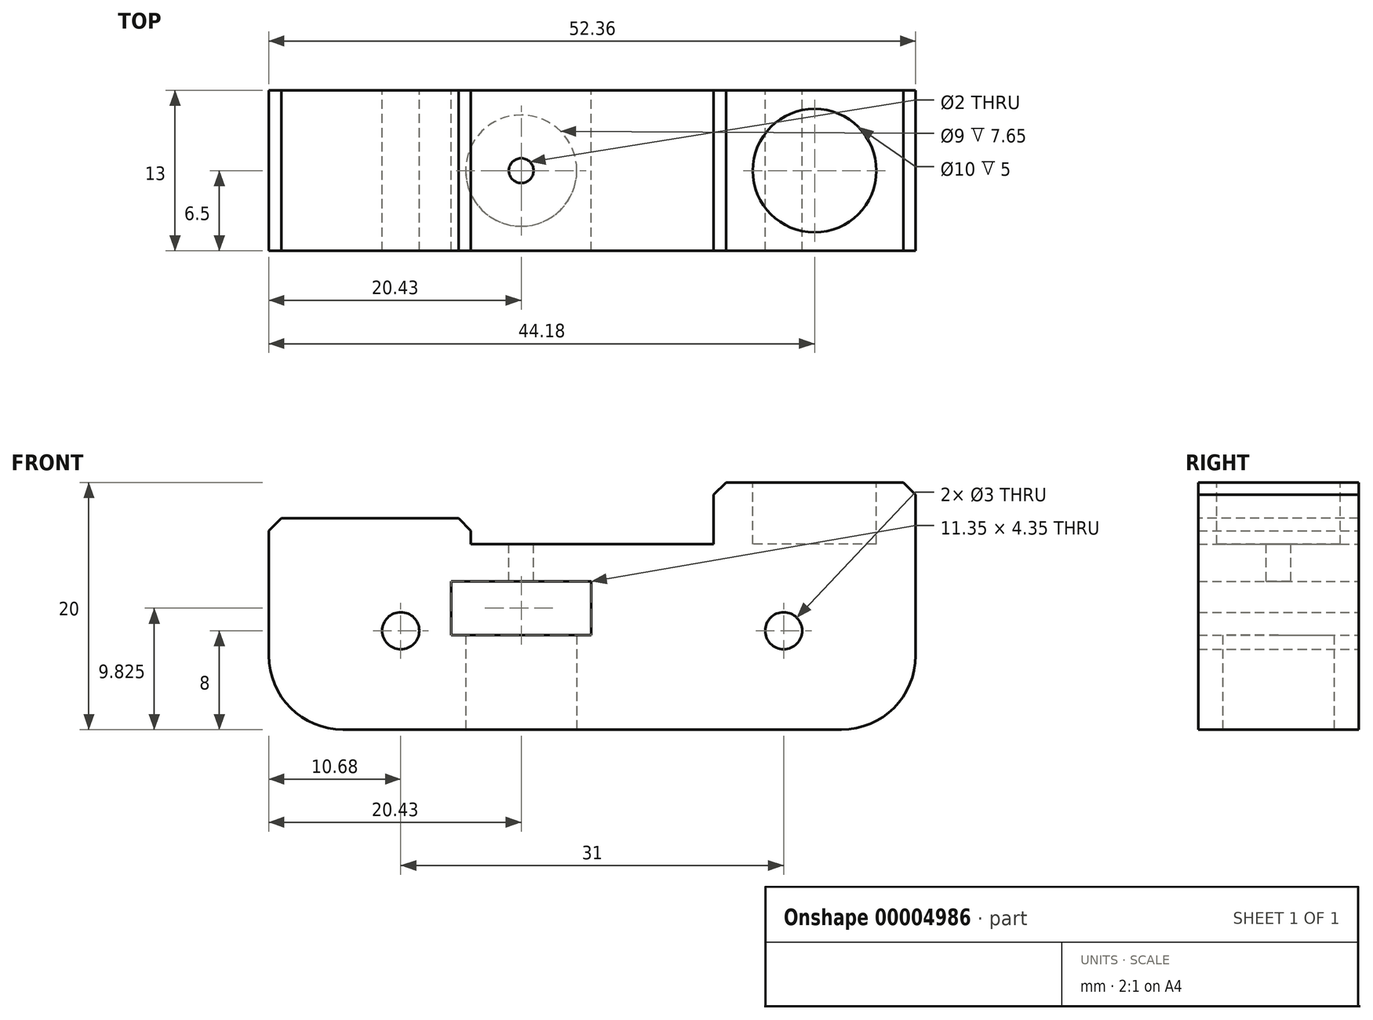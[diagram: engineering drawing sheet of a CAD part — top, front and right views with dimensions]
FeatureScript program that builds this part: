
annotation { "Feature Type Name" : "Feature", "Feature Type Description" : "" }
export const myFeature = defineFeature(function(context is Context, id is Id, definition is map)
    precondition{}
    {
        {
            var Q0;
            Q0=qCreatedBy(makeId("Front.planeOp"),FACE);
            var sketch = newSketch(context, id + "F0", { "sketchPlane" : qUnion([Q0])});
            skLineSegment(sketch, "E0", {"start": v(0, 0) * mm, "end": v(31, 0) * mm, "construction": true});
            skLineSegment(sketch, "E1", {"start": v(0, 0) * mm, "end": v(0, 31) * mm, "construction": true});
            skPoint(sketch, "E2", {"position": v(0, 10.1) * mm});
            skCircle(sketch, "E3", {"center": v(0, 0) * mm, "radius": 1.5 * mm});
            skCircle(sketch, "E4", {"center": v(31, 0) * mm, "radius": 1.5 * mm});
            skLineSegment(sketch, "E5", {"start": v(15.5, 0) * mm, "end": v(15.5, 31) * mm, "construction": true});
            skLineSegment(sketch, "E6", {"start": v(9.75, 0) * mm, "end": v(9.75, 33.75) * mm, "construction": true});
            skArc(sketch, "E7", {"start": v(0, 10.1) * mm, "mid": v(17.8, 20.04) * mm, "end": v(18.66, 40.41) * mm, "construction": true});
            skLineSegment(sketch, "E8", {"start": v(33.5, 41.53) * mm, "end": v(33.5, -19.25) * mm, "construction": true});
            skCircle(sketch, "E9", {"center": v(15.5, 15.5) * mm, "radius": 7.5 * mm, "construction": true});
            skLineSegment(sketch, "E10", {"start": v(-10.68, 9.1) * mm, "end": v(5.67, 9.1) * mm});
            skLineSegment(sketch, "E11", {"start": v(5.67, 9.1) * mm, "end": v(5.67, 7) * mm});
            skLineSegment(sketch, "E12", {"start": v(5.67, 7) * mm, "end": v(25.32, 7) * mm});
            skLineSegment(sketch, "E13", {"start": v(25.32, 7) * mm, "end": v(25.32, 12) * mm});
            skLineSegment(sketch, "E14", {"start": v(25.32, 12) * mm, "end": v(41.68, 12) * mm});
            skPoint(sketch, "E15", {"position": v(33.5, 12) * mm});
            skLineSegment(sketch, "E16", {"start": v(-10.68, 9.1) * mm, "end": v(-10.68, -8) * mm});
            skLineSegment(sketch, "E17", {"start": v(-10.68, -8) * mm, "end": v(41.68, -8) * mm});
            skLineSegment(sketch, "E18", {"start": v(41.68, -8) * mm, "end": v(41.68, 12) * mm});
            skPoint(sketch, "E19", {"position": v(15.5, 8) * mm});
            skLineSegment(sketch, "E20.bottom", {"start": v(4.08, 4) * mm, "end": v(15.42, 4) * mm});
            skLineSegment(sketch, "E20.top", {"start": v(4.08, -0.35) * mm, "end": v(15.42, -0.35) * mm});
            skLineSegment(sketch, "E20.left", {"start": v(4.08, 4) * mm, "end": v(4.08, -0.35) * mm});
            skLineSegment(sketch, "E20.right", {"start": v(15.43, 4) * mm, "end": v(15.43, -0.35) * mm});
            skSolve(sketch);
        }
        {
            var Q0;
            Q0 = qSketchRegion(id + "F0", true);
            extrude(context, id + "F1", {"entities" : qUnion([Q0]), "depth" : 13 * mm, "symmetric" : true});
        }
        {
            var Q0;
            Q0=makeQuery(id+"F1.opExtrude","SWEPT_FACE",FACE,{"disambiguationData":[OSD([sQuery(id+"F0.wireOp",EDGE,"E12")])]});
            var sketch = newSketch(context, id + "F2", { "sketchPlane" : qUnion([Q0])});
            skLineSegment(sketch, "E21.0", {"start": v(4.08, -6.5) * mm, "end": v(15.43, -6.5) * mm, "construction": true});
            skLineSegment(sketch, "E22", {"start": v(9.75, -6.5) * mm, "end": v(9.75, 6.5) * mm, "construction": true});
            skCircle(sketch, "E23", {"center": v(9.75, 0) * mm, "radius": 1 * mm});
            skSolve(sketch);
        }
        {
            var Q0;
            Q0 = qSketchRegion(id + "F2", true);
            extrude(context, id + "F3", {"entities" : qUnion([Q0]), "operationType" : NewBodyOperationType.REMOVE, "endBound" : BoundingType.THROUGH_ALL, "oppositeDirection" : true, "depth" : 25 * mm});
        }
        {
            var Q0;
            Q0=makeQuery(id+"F1.opExtrude","SWEPT_FACE",FACE,{"disambiguationData":[OSD([sQuery(id+"F0.wireOp",EDGE,"E17")])]});
            var sketch = newSketch(context, id + "F4", { "sketchPlane" : qUnion([Q0])});
            skCircle(sketch, "E24", {"center": v(9.75, 0) * mm, "radius": 4.5 * mm});
            skSolve(sketch);
        }
        {
            var Q0;
            Q0 = qSketchRegion(id + "F4", true);
            var Q1;
            Q1=makeQuery(id+"F1.opExtrude","SWEPT_FACE",FACE,{"disambiguationData":[OSD([sQuery(id+"F0.wireOp",EDGE,"E20.top")])]});
            extrude(context, id + "F5", {"entities" : qUnion([Q0]), "operationType" : NewBodyOperationType.REMOVE, "endBound" : BoundingType.UP_TO_SURFACE, "oppositeDirection" : true, "endBoundEntityFace" : qUnion([Q1]), "depth" : 25 * mm});
        }
        {
            var Q0;
            Q0=makeQuery(id+"F3.boolean.opBoolean","COPY",EDGE,{"derivedFrom":makeQuery(id+"F3.opExtrude","CAP_EDGE",EDGE,{"disambiguationData":[OSD([sQuery(id+"F2.wireOp",EDGE,"E23")])],"isStart":true})});
            var Q1;
            Q1=makeQuery(id+"F5.boolean.opBoolean","COPY",EDGE,{"derivedFrom":makeQuery(id+"F5.opExtrude","CAP_EDGE",EDGE,{"disambiguationData":[OSD([sQuery(id+"F4.wireOp",EDGE,"E24")])],"isStart":true})});
            var Q2;
            Q2=makeQuery(id+"F1.opExtrude","SWEPT_EDGE",EDGE,{"disambiguationData":[OSD([sQuery(id+"F0.wireOp",EDGE,"E10"),sQuery(id+"F0.wireOp",EDGE,"E11")])]});
            var Q3;
            Q3=makeQuery(id+"F1.opExtrude","SWEPT_EDGE",EDGE,{"disambiguationData":[OSD([sQuery(id+"F0.wireOp",EDGE,"E13"),sQuery(id+"F0.wireOp",EDGE,"E14")])]});
            var Q4;
            Q4=makeQuery(id+"F1.opExtrude","SWEPT_EDGE",EDGE,{"disambiguationData":[OSD([sQuery(id+"F0.wireOp",EDGE,"E10"),sQuery(id+"F0.wireOp",EDGE,"E16")])]});
            var Q5;
            Q5=makeQuery(id+"F1.opExtrude","SWEPT_EDGE",EDGE,{"disambiguationData":[OSD([sQuery(id+"F0.wireOp",EDGE,"E14"),sQuery(id+"F0.wireOp",EDGE,"E18")])]});
            chamfer(context, id + "F6", {"entities" : qUnion([Q0, Q1, Q2, Q3, Q4, Q5]), "width" : 1 * mm, "tangentPropagation" : true});
        }
        {
            var Q0;
            Q0=makeQuery(id+"F1.opExtrude","SWEPT_EDGE",EDGE,{"disambiguationData":[OSD([sQuery(id+"F0.wireOp",EDGE,"E16"),sQuery(id+"F0.wireOp",EDGE,"E17")])]});
            var Q1;
            Q1=makeQuery(id+"F1.opExtrude","SWEPT_EDGE",EDGE,{"disambiguationData":[OSD([sQuery(id+"F0.wireOp",EDGE,"E17"),sQuery(id+"F0.wireOp",EDGE,"E18")])]});
            fillet(context, id + "F7", {"entities" : qUnion([Q0, Q1]), "radius" : 6 * mm, "tangentPropagation" : true, "allowEdgeOverflow" : false});
        }
        {
            var Q0;
            Q0=makeQuery(id+"F1.opExtrude","SWEPT_FACE",FACE,{"disambiguationData":[OSD([sQuery(id+"F0.wireOp",EDGE,"E14")])]});
            var sketch = newSketch(context, id + "F8", { "sketchPlane" : qUnion([Q0])});
            skLineSegment(sketch, "E25", {"start": v(33.5, 6.5) * mm, "end": v(33.5, -6.5) * mm, "construction": true});
            skCircle(sketch, "E26", {"center": v(33.5, 0) * mm, "radius": 5 * mm});
            skSolve(sketch);
        }
        {
            var Q0;
            Q0 = qSketchRegion(id + "F8", true);
            extrude(context, id + "F9", {"entities" : qUnion([Q0]), "operationType" : NewBodyOperationType.REMOVE, "oppositeDirection" : true, "depth" : 5 * mm});
        }
    });
